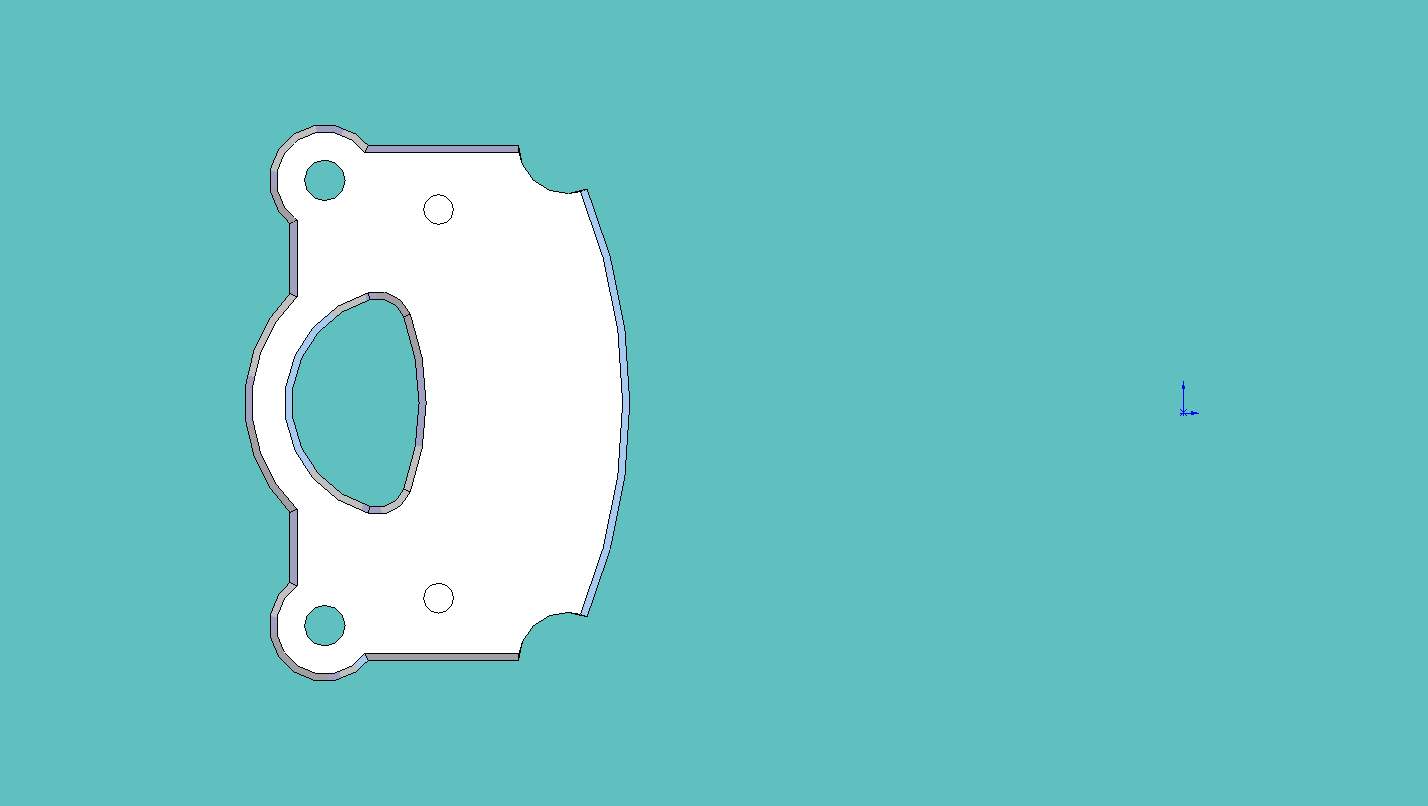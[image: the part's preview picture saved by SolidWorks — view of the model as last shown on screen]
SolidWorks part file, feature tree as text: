
SOLIDWORKS PART (.sldprt)
format: sldprt  version: not decoded by parser v0  size: 278,528 bytes
history: native  units: mm
features: sketch x5, cut_extrude x4, material x1, extrude x1 (+13 scaffold rows collapsed)
feature tree (24):
  scaffold x13  (default folders/planes/origin — collapsed)
  material  "Material <not specified>"
  sketch  "Sketch1"  dims[D1=7.62mm]
  extrude  "Extrude1"  Depth=17.78mm
  sketch  "Sketch3"  dims[D1=8.89mm]
  cut_extrude  "Cut-Extrude2"  [1 undecoded]
  sketch  "Sketch4"  dims[D1=7.62mm]
  cut_extrude  "Cut-Extrude3"  [1 undecoded]
  sketch  "Sketch5"
  cut_extrude  "Cut-Extrude4"  Depth=26.162mm
  sketch  "Sketch6"  dims[D1=6.5278mm]
  cut_extrude  "Cut-Extrude5"  Depth=7.62mm
decode coverage: 7 of 10 modeling features carry decoded parameters
note: 2 parameter values undecoded
note: suppression state not decoded; provenance and decode notes live in map.json
